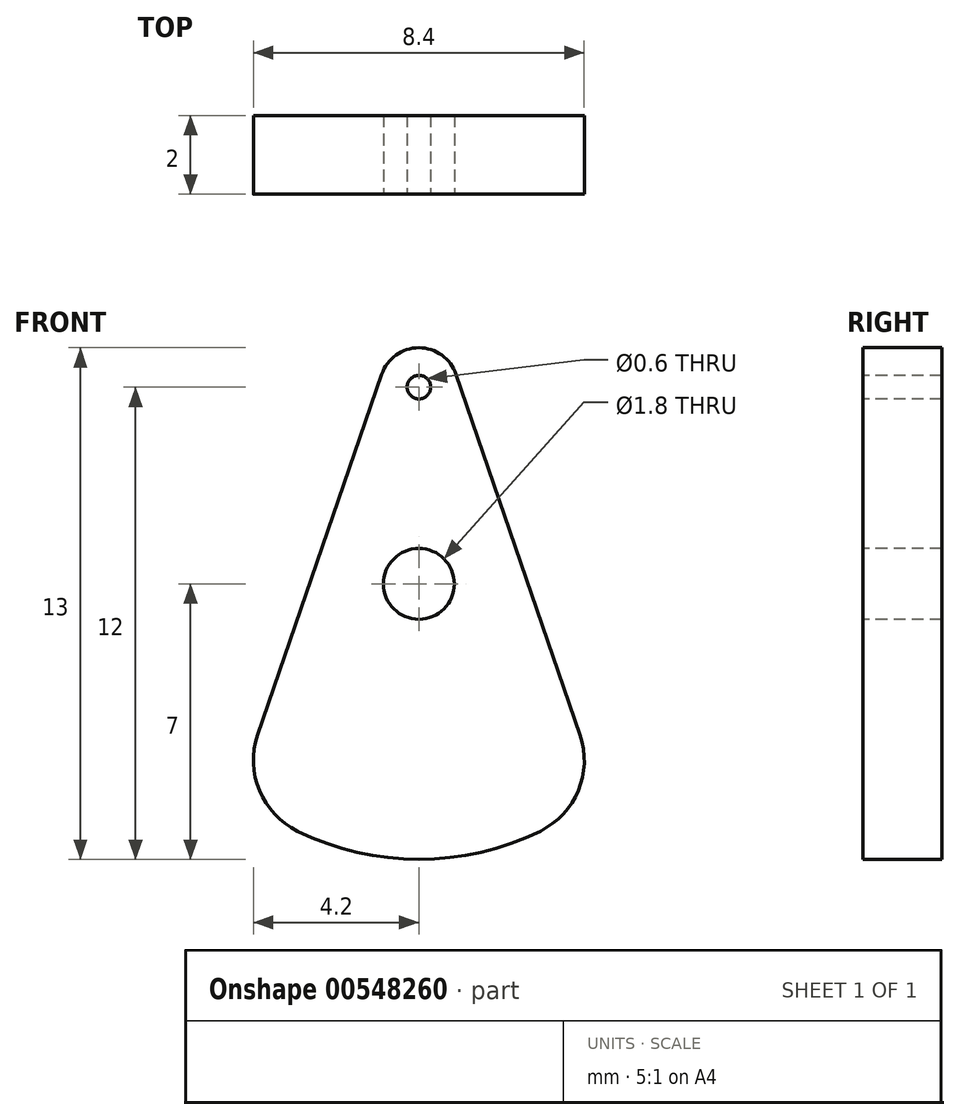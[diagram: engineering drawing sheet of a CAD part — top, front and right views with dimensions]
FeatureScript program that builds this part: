
annotation { "Feature Type Name" : "Feature", "Feature Type Description" : "" }
export const myFeature = defineFeature(function(context is Context, id is Id, definition is map)
    precondition{}
    {
        {
            var Q0;
            Q0=qCreatedBy(makeId("Front.planeOp"),FACE);
            var sketch = newSketch(context, id + "F0", { "sketchPlane" : qUnion([Q0])});
            skCircle(sketch, "E0", {"center": v(0, 5) * mm, "radius": 1 * mm});
            skLineSegment(sketch, "E1", {"start": v(-0.95, 5.33) * mm, "end": v(-4.6, -5.28) * mm});
            skLineSegment(sketch, "E2", {"start": v(0.95, 5.33) * mm, "end": v(4.6, -5.28) * mm});
            skArc(sketch, "E3", {"start": v(-4.6, -5.28) * mm, "mid": v(0, -7) * mm, "end": v(4.6, -5.28) * mm});
            skSolve(sketch);
        }
        {
            var Q0;
            {var subQ0=sQuery(id+"F0.wireOp",EDGE,"E0");var subQ1=makeQuery(id+"F0.imprint","INTERSECT",VERTEX,{"derivedFrom":[subQ0,sQuery(id+"F0.wireOp",EDGE,"w8e6eGdO-ENVF-9NGL-huWQ-efc06CgisPO5")]});Q0=makeQuery(id+"F0.imprint","IMPRINT",FACE,{"disambiguationData":[TD([[makeQuery(id+"F0.imprint","IMPRINT",EDGE,{"disambiguationData":[TD([[subQ1,-1.0]])],"derivedFrom":subQ0}),1.0]])]});}
            var Q1;
            Q1=makeQuery(id+"F0.imprint","IMPRINT",FACE,{"disambiguationData":[TD([[makeQuery(id+"F0.imprint","IMPRINT",EDGE,{"derivedFrom":sQuery(id+"F0.wireOp",EDGE,"qOYSfqBt-NmhD-NmtI-VSbv-XXUutc5HEYni")}),1.0]])]});
            var Q2;
            {var subQ0=sQuery(id+"F0.wireOp",EDGE,"E1");Q2=makeQuery(id+"F0.imprint","IMPRINT",FACE,{"disambiguationData":[TD([[makeQuery(id+"F0.imprint","IMPRINT",EDGE,{"derivedFrom":subQ0}),1.0]])]});}
            extrude(context, id + "F1", {"entities" : qUnion([Q0, Q1, Q2]), "endBound" : BoundingType.SYMMETRIC, "oppositeDirection" : true, "depth" : 2 * mm, "offsetDistance" : 25 * mm});
        }
        {
            var Q0;
            Q0=makeQuery(id+"F1.opExtrude","CAP_FACE",FACE,{"disambiguationData":[OSD([sQuery(id+"F0.wireOp",EDGE,"qOYSfqBt-NmhD-NmtI-VSbv-XXUutc5HEYni"),sQuery(id+"F0.wireOp",EDGE,"E0"),sQuery(id+"F0.wireOp",EDGE,"w8e6eGdO-ENVF-9NGL-huWQ-efc06CgisPO5"),sQuery(id+"F0.wireOp",EDGE,"iYMXR5ba-jJtk-YTGX-zwfv-GuyQTSMkrF53"),sQuery(id+"F0.wireOp",EDGE,"8fa9d855-14f8-4af0-bdf3-113db9f97734.filletArc"),sQuery(id+"F0.wireOp",EDGE,"f835260d-c7fa-4381-84e8-d9dfa970b7f8.filletArc")])],"isStart":true});
            var sketch = newSketch(context, id + "F2", { "sketchPlane" : qUnion([Q0])});
            skCircle(sketch, "E4", {"center": v(0, 0) * mm, "radius": 0.9 * mm});
            skCircle(sketch, "E5", {"center": v(0, 5) * mm, "radius": 0.3 * mm});
            skSolve(sketch);
        }
        {
            var Q0;
            Q0 = qSketchRegion(id + "F2", true);
            extrude(context, id + "F3", {"entities" : qUnion([Q0]), "operationType" : NewBodyOperationType.REMOVE, "endBound" : BoundingType.THROUGH_ALL, "oppositeDirection" : true, "depth" : 25 * mm, "offsetDistance" : 25 * mm});
        }
        {
            var Q0;
            Q0=makeQuery(id+"F1.opExtrude","SWEPT_EDGE",EDGE,{"disambiguationData":[OSD([sQuery(id+"F0.wireOp",EDGE,"E2"),sQuery(id+"F0.wireOp",EDGE,"E3")])]});
            var Q1;
            Q1=makeQuery(id+"F1.opExtrude","SWEPT_EDGE",EDGE,{"disambiguationData":[OSD([sQuery(id+"F0.wireOp",EDGE,"E1"),sQuery(id+"F0.wireOp",EDGE,"E3")])]});
            fillet(context, id + "F4", {"entities" : qUnion([Q0, Q1]), "radius" : 2 * mm, "tangentPropagation" : true, "allowEdgeOverflow" : false});
        }
    });
